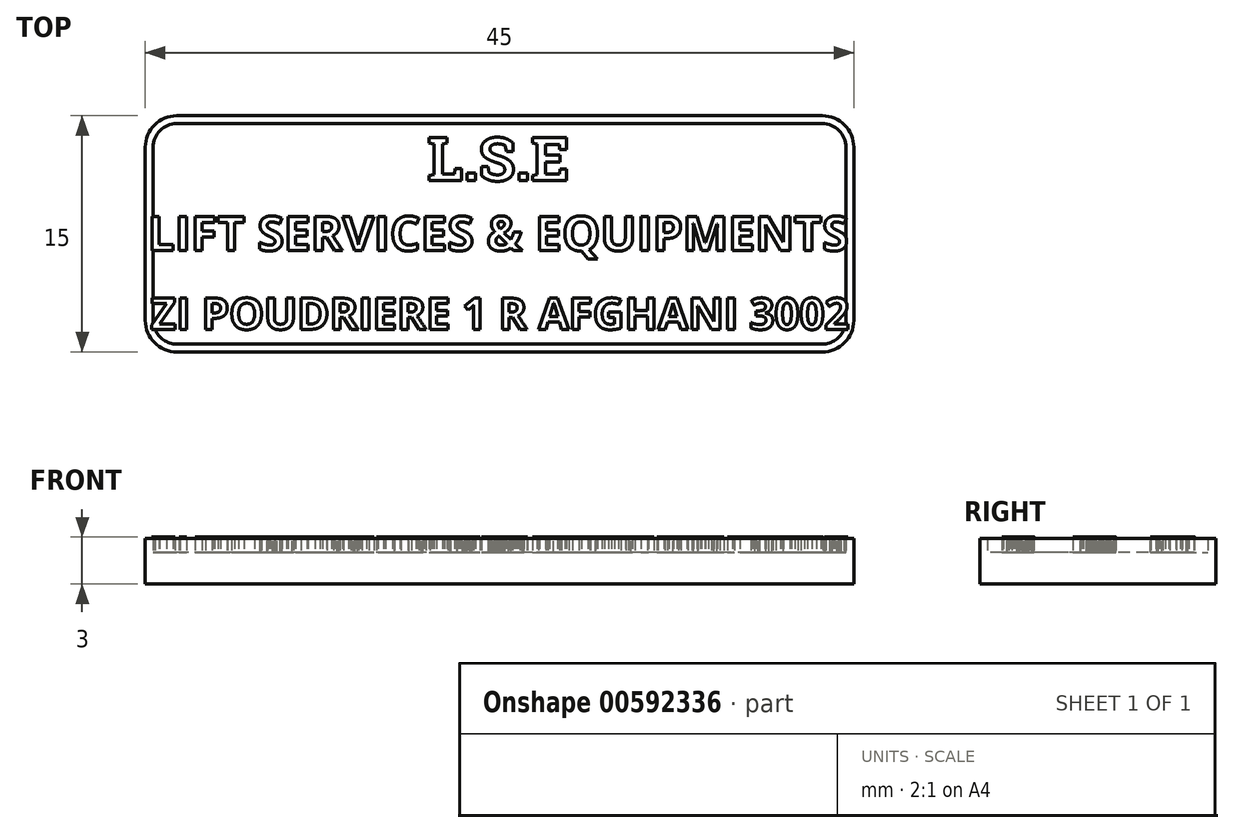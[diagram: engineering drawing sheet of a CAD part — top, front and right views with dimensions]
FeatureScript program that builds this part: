
annotation { "Feature Type Name" : "Feature", "Feature Type Description" : "" }
export const myFeature = defineFeature(function(context is Context, id is Id, definition is map)
    precondition{}
    {
        {
            var Q0;
            Q0=qCreatedBy(makeId("Top.planeOp"),FACE);
            var sketch = newSketch(context, id + "F0", { "sketchPlane" : qUnion([Q0])});
            skLineSegment(sketch, "E0.bottom", {"start": v(20.5, 7.5) * mm, "end": v(-20.5, 7.5) * mm});
            skLineSegment(sketch, "E0.top", {"start": v(20.5, -7.5) * mm, "end": v(-20.5, -7.5) * mm});
            skLineSegment(sketch, "E0.left", {"start": v(22.5, 5.5) * mm, "end": v(22.5, -5.5) * mm});
            skLineSegment(sketch, "E0.right", {"start": v(-22.5, 5.5) * mm, "end": v(-22.5, -5.5) * mm});
            skPoint(sketch, "E0.middle", {"position": v(0, 0) * mm});
            skPoint(sketch, "E1.visualSharp", {"position": v(-22.5, 7.5) * mm});
            skArc(sketch, "E1.filletArc", {"start": v(-20.5, 7.5) * mm, "mid": v(-21.91, 6.91) * mm, "end": v(-22.5, 5.5) * mm});
            skPoint(sketch, "E2.visualSharp", {"position": v(-22.5, -7.5) * mm});
            skArc(sketch, "E2.filletArc", {"start": v(-22.5, -5.5) * mm, "mid": v(-21.91, -6.91) * mm, "end": v(-20.5, -7.5) * mm});
            skPoint(sketch, "E3.visualSharp", {"position": v(22.5, -7.5) * mm});
            skArc(sketch, "E3.filletArc", {"start": v(20.5, -7.5) * mm, "mid": v(21.91, -6.91) * mm, "end": v(22.5, -5.5) * mm});
            skPoint(sketch, "E4.visualSharp", {"position": v(22.5, 7.5) * mm});
            skArc(sketch, "E4.filletArc", {"start": v(22.5, 5.5) * mm, "mid": v(21.91, 6.91) * mm, "end": v(20.5, 7.5) * mm});
            skSolve(sketch);
        }
        {
            var Q0;
            Q0=qCreatedBy(makeId("Top.planeOp"),FACE);
            var sketch = newSketch(context, id + "F1", { "sketchPlane" : qUnion([Q0])});
            skText(sketch, "E5", { "text": "ZI POUDRIERE 1 R AFGHANI 3002", "fontName": "OpenSans-Bold.ttf"});
            const initialGuessF1  = {"E5": [-0.02216, -0.00607, 1, 0, 0.002]};
            skSetInitialGuess(sketch, initialGuessF1);
            skSolve(sketch);
        }
        {
            var Q0;
            Q0=qCreatedBy(makeId("Top.planeOp"),FACE);
            var sketch = newSketch(context, id + "F2", { "sketchPlane" : qUnion([Q0])});
            skText(sketch, "E6", { "text": "LIFT SERVICES & EQUIPMENTS", "fontName": "OpenSans-Bold.ttf"});
            const initialGuessF2  = {"E6": [-0.02235, -0.00107, 1, 0, 0.0022]};
            skSetInitialGuess(sketch, initialGuessF2);
            skSolve(sketch);
        }
        {
            var Q0;
            Q0=qCreatedBy(makeId("Top.planeOp"),FACE);
            var sketch = newSketch(context, id + "F3", { "sketchPlane" : qUnion([Q0])});
            skText(sketch, "E7", { "text": "L.S.E", "fontName": "RobotoSlab-Bold.ttf"});
            const initialGuessF3  = {"E7": [-0.00457, 0.00337, 1, 0, 0.00277]};
            skSetInitialGuess(sketch, initialGuessF3);
            skSolve(sketch);
        }
        {
            var Q0;
            Q0=makeQuery(id+"F0.imprint","IMPRINT",FACE,{"disambiguationData":[TD([[makeQuery(id+"F0.imprint","IMPRINT",EDGE,{"derivedFrom":sQuery(id+"F0.wireOp",EDGE,"E0.bottom")}),1.0]])]});
            extrude(context, id + "F4", {"entities" : qUnion([Q0]), "oppositeDirection" : true, "depth" : 2 * mm, "hasOffset" : true, "offsetDistance" : 25 * mm, "offsetOppositeDirection" : true});
        }
        {
            var Q0;
            Q0 = qSketchRegion(id + "F3", true);
            var Q1;
            Q1 = qSketchRegion(id + "F2", true);
            var Q2;
            Q2 = qSketchRegion(id + "F1", true);
            extrude(context, id + "F5", {"entities" : qUnion([Q0, Q1, Q2]), "operationType" : NewBodyOperationType.ADD, "depth" : 1 * mm, "offsetDistance" : 25 * mm});
        }
        {
            var Q0;
            Q0=qCreatedBy(makeId("Top.planeOp"),FACE);
            var sketch = newSketch(context, id + "F6", { "sketchPlane" : qUnion([Q0])});
            skArc(sketch, "E8.0", {"start": v(22.5, 5.5) * mm, "mid": v(21.91, 6.91) * mm, "end": v(20.5, 7.5) * mm});
            skLineSegment(sketch, "E8.1", {"start": v(22.5, 5.5) * mm, "end": v(22.5, -5.5) * mm});
            skLineSegment(sketch, "E8.2", {"start": v(20.5, 7.5) * mm, "end": v(-20.5, 7.5) * mm});
            skArc(sketch, "E8.3", {"start": v(20.5, -7.5) * mm, "mid": v(21.91, -6.91) * mm, "end": v(22.5, -5.5) * mm});
            skArc(sketch, "E8.4", {"start": v(-20.5, 7.5) * mm, "mid": v(-21.91, 6.91) * mm, "end": v(-22.5, 5.5) * mm});
            skLineSegment(sketch, "E8.5", {"start": v(-22.5, 5.5) * mm, "end": v(-22.5, -5.5) * mm});
            skArc(sketch, "E8.6", {"start": v(-22.5, -5.5) * mm, "mid": v(-21.91, -6.91) * mm, "end": v(-20.5, -7.5) * mm});
            skLineSegment(sketch, "E8.7", {"start": v(20.5, -7.5) * mm, "end": v(-20.5, -7.5) * mm});
            skArc(sketch, "E9.0", {"start": v(22, 5.5) * mm, "mid": v(21.56, 6.56) * mm, "end": v(20.5, 7) * mm});
            skLineSegment(sketch, "E9.1", {"start": v(22, 5.5) * mm, "end": v(22, -5.5) * mm});
            skLineSegment(sketch, "E9.2", {"start": v(20.5, 7) * mm, "end": v(-20.5, 7) * mm});
            skArc(sketch, "E9.3", {"start": v(20.5, -7) * mm, "mid": v(21.56, -6.56) * mm, "end": v(22, -5.5) * mm});
            skArc(sketch, "E9.4", {"start": v(-20.5, 7) * mm, "mid": v(-21.56, 6.56) * mm, "end": v(-22, 5.5) * mm});
            skLineSegment(sketch, "E9.5", {"start": v(-22, 5.5) * mm, "end": v(-22, -5.5) * mm});
            skArc(sketch, "E9.6", {"start": v(-22, -5.5) * mm, "mid": v(-21.56, -6.56) * mm, "end": v(-20.5, -7) * mm});
            skLineSegment(sketch, "E9.7", {"start": v(20.5, -7) * mm, "end": v(-20.5, -7) * mm});
            skSolve(sketch);
        }
        {
            var Q0;
            Q0 = qSketchRegion(id + "F6", true);
            extrude(context, id + "F7", {"entities" : qUnion([Q0]), "operationType" : NewBodyOperationType.ADD, "depth" : 0.9 * mm, "offsetDistance" : 25 * mm});
        }
    });
